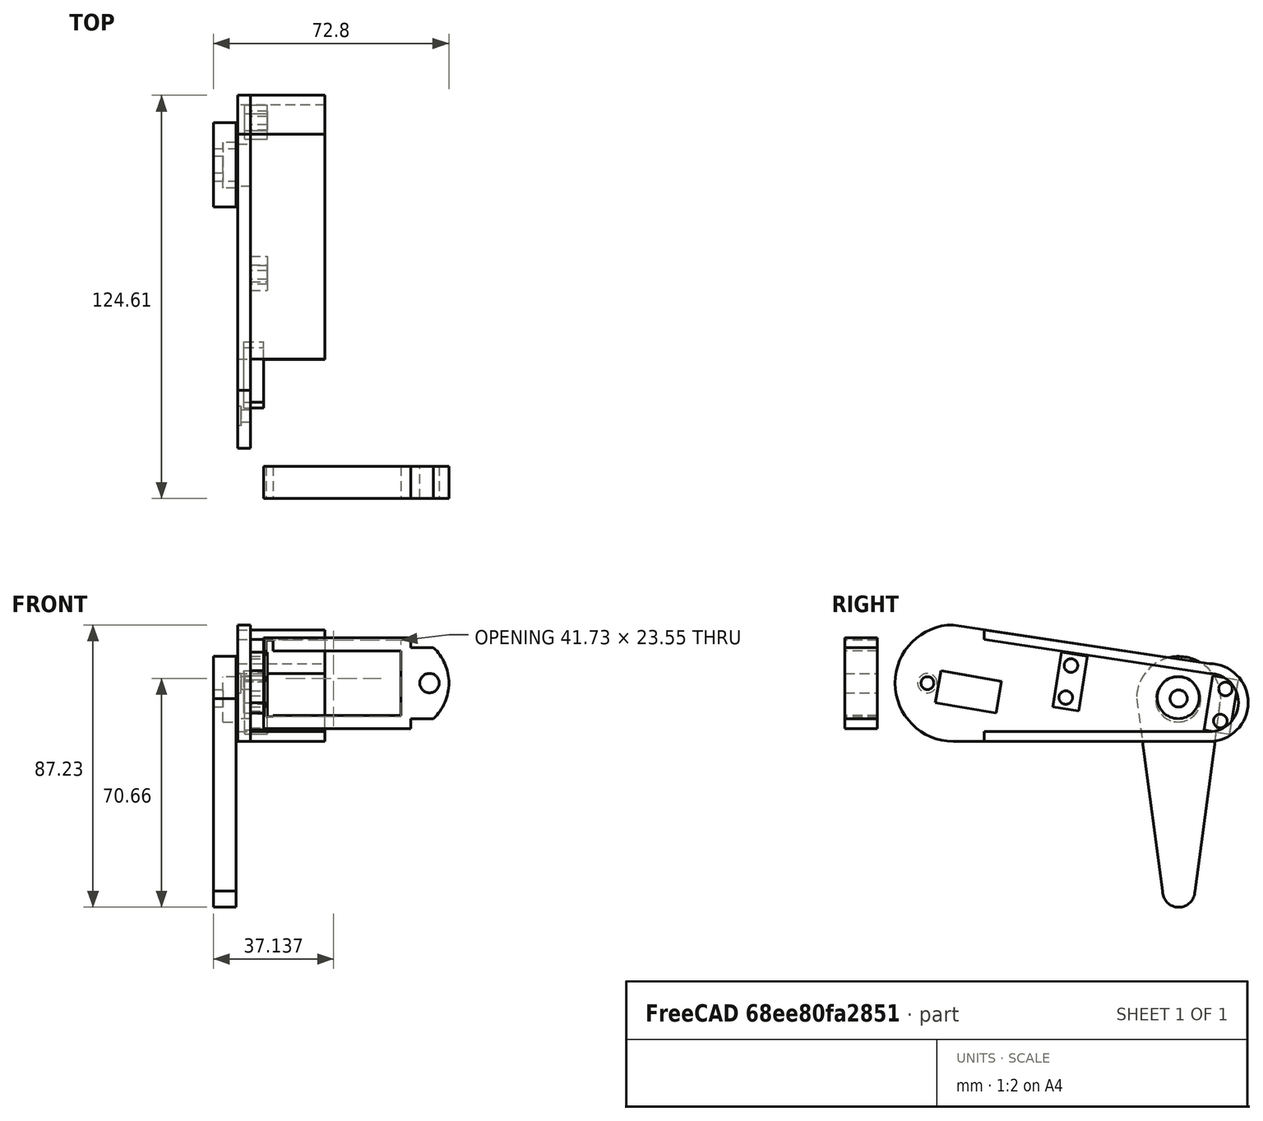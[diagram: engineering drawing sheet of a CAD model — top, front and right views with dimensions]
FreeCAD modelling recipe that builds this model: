
FCSTD DOCUMENT  (FreeCAD 0.20R29603 (Git))
Label: perro
License: All rights reserved
LicenseURL: http://en.wikipedia.org/wiki/All_rights_reserved
objects: Part::Cylinder×8, PartDesign::Pad×5, App::DocumentObjectGroup×5, Part::Cut×5, Sketcher::SketchObject×4, PartDesign::Body×4, Part::MultiFuse×4, Part::Box×4, Mesh::Feature×3, Spreadsheet::Sheet×1
note: 39 computed .brp shape members not serialized (recipe doc carries the construction recipe); baked Part::Feature solids carry a one-line shape summary decoded from their .brp

FEATURE [Mesh::Feature] nema17v0
  Placement = pos=(56,-128,65) rot=(-1,0,0;1.5708rad)
FEATURE [Sketcher::SketchObject] Sketch
  FullyConstrained = false
  MapMode = 5
  Placement = pos=(0,0,0) rot=(0.57735,0.57735,0.57735;2.0944rad)
  Support = -> [YZ_Plane]
  expr: Constraints[10] = Spreadsheet.AnchoPata
  expr: Constraints[12] = Spreadsheet.AnchoPata * 2
  expr: Constraints[14] = Spreadsheet.LargoRodillaExterior
  expr: Constraints[3] = Spreadsheet.AnchoRodilla
  expr: Constraints[5] = Spreadsheet.AnchoRodilla * 2
  sketch-geometry (5):
    g0: Circle CenterX=25.5525 CenterY=39.037 CenterZ=0 NormalX=0 NormalY=0 NormalZ=1 AngleXU=0 Radius=2.6446
    g1: LineSegment StartX=12.5525 StartY=39.0371 StartZ=0 EndX=20.5525 EndY=-20.4272 EndZ=0
    g2: LineSegment StartX=30.5525 StartY=-20.4272 StartZ=0 EndX=38.5525 EndY=39.0371 EndZ=0
    g3: ArcOfCircle CenterX=25.5525 CenterY=39.037 CenterZ=0 NormalX=0 NormalY=0 NormalZ=1 AngleXU=0 Radius=13 StartAngle=3.539e-06 EndAngle=3.14159
    g4: ArcOfCircle CenterX=25.5525 CenterY=-20.4272 CenterZ=0 NormalX=0 NormalY=0 NormalZ=1 AngleXU=0 Radius=5 StartAngle=3.1416 EndAngle=6.28318
  constraints (15):
    c: Coincident(g3,g1)
    c: Coincident(g3,g2)
    c: Coincident(g0,g3)
    c: Radius(g3) = 13
    c: Horizontal(g2,g1)
    c: DistanceX(g1,g2) = 26
    c: DistanceX(g0) = 25.5525
    c: DistanceY(g0) = 39.037
    c: Coincident(g4,g1)
    c: Coincident(g4,g2)
    c: Radius(g4) = 5
    c: Horizontal(g1,g2)
    c: DistanceX(g1,g2) = 10
    c: Equal(g2,g1)
    c: Distance(g2) = 60
FEATURE [PartDesign::Pad] Pad
  Direction = (1,-2e-16,3e-16)
  Length = 7
  Length2 = 10
  Placement = pos=(0,0,0) rot=(0.57735,0.57735,0.57735;2.0944rad)
  Profile = -> Sketch
  ReferenceAxis = -> Sketch [N_Axis]
  Type = 0
FEATURE [PartDesign::Body] Body  label="DebajoRodilla"
  Group = -> [Sketch,Pad]
  Origin = -> Origin
  Placement = pos=(10.5,-0.4,0.2) rot=(0,0,1;0rad)
  Tip = -> Pad
FEATURE [Spreadsheet::Sheet] Spreadsheet
  cells = A1=LargoParedesTrapecio; B1(LargoParedesTrapecio)=3; A2=RadioPataBase; B2(RadioPataBase)=12; D2=AnchoRodilla; E2(AnchoRodilla)=13; G2=LargoPiernaExterior; H2(LargoPiernaExterior)=20; J2=PiernaPiernaLargoExterior; K2(PiernaPiernaLargoExterior)=72; A3=RadioArcoInterior; B3(RadioArcoInterior)=15; D3=LargoRodillaExterior; E3(LargoRodillaExterior)=60; G3=LargoPiernaInterior; H3(LargoPiernaInterior)=20; J3=PiernaPiernaLargoInterior; K3(PiernaPiernaLargoInterior)=80; A4=AnchoPie; B4(AnchoPie)=17; D4=LargoRodillaInterior; E4(LargoRodillaInterior)=40; G4=AnchoPierna; H4(AnchoPierna)=15; J4=RadioPiernaSuperior; K4(RadioPiernaSuperior)=18; A5=LargoPieExterior; B5(LargoPieExterior)=10; D5=AnguloRodillaExterior; E5(AnguloRodillaExterior)=150; G5=RadioPierna; H5(RadioPierna)=9; J5=RadioPiernaInferior; K5(RadioPiernaInferior)=12; A6=LargoPieInterior; B6(LargoPieInterior)=10; D6=AnguloRodillaInterior; E6(AnguloRodillaInterior)=130; J6=AnguloPierna; K6(AnguloPierna)=20; A7=AnguloInteriorPie; B7(AnguloInteriorPie)=130; D7=AnchoPata; E7(AnchoPata)=5; A8=AnguloExteriorPie; B8(AnguloExteriorPie)=-150; A9=AnguloInteriorTrapecioPie; B9(AnguloInteriorTrapecioPie)=110; A10=BaseMenorTrapecio; B10(BaseMenorTrapecio)=7; A11=BaseMayorTrapecio; B11(BaseMayorTrapecio)=10; A12=DisTrapBaseMenACentCir; B12(DisTrapBaseMenACentCir)=20
FEATURE [Sketcher::SketchObject] Sketch002
  FullyConstrained = false
  MapMode = 5
  Placement = pos=(0,0,0) rot=(0.57735,0.57735,0.57735;2.0944rad)
  Support = -> [YZ_Plane002]
  expr: Constraints[10] = Spreadsheet.RadioPiernaInferior
  expr: Constraints[8] = Spreadsheet.PiernaPiernaLargoInterior
  expr: Constraints[9] = Spreadsheet.RadioPiernaSuperior
  sketch-geometry (9):
    g0: LineSegment StartX=-19.4851 StartY=0 StartZ=0 EndX=59.6098 EndY=0 EndZ=0
    g1: LineSegment StartX=-19.4851 StartY=36 StartZ=0 EndX=59.6098 EndY=24 EndZ=0
    g2: ArcOfCircle CenterX=59.6098 CenterY=12 CenterZ=0 NormalX=0 NormalY=0 NormalZ=1 AngleXU=0 Radius=12 StartAngle=4.71239 EndAngle=7.85398
    g3: ArcOfCircle CenterX=-19.4851 CenterY=18 CenterZ=0 NormalX=0 NormalY=0 NormalZ=1 AngleXU=0 Radius=18 StartAngle=1.5708 EndAngle=4.71239
    g4: Circle CenterX=50 CenterY=13.5287 CenterZ=0 NormalX=0 NormalY=0 NormalZ=1 AngleXU=0 Radius=6.5
    g5: GeomPoint X=68.8344 Y=19.675 Z=0
    g6: GeomPoint X=66.0715 Y=1.88833 Z=0
    g7: Circle CenterX=-27.4851 CenterY=18 CenterZ=0 NormalX=0 NormalY=0 NormalZ=1 AngleXU=0 Radius=1.98925
    g8: GeomPoint X=-37.4851 Y=18 Z=0
  constraints (25):
    c: Coincident(g2,g1)
    c: Coincident(g3,g1)
    c: Coincident(g3,g0)
    c: Vertical(g2,g1)
    c: Coincident(g2,g0)
    c: Vertical(g3,g1)
    c: Vertical(g3,g0)
    c: Vertical(g2,g0)
    c: Distance(g1) = 80
    c: Radius(g3) = 18
    c: Radius(g2) = 12
    c: PointOnObject(g0,g-1)
    c: PointOnObject(g0,g-1)
    c: Angle(g1,g-1) = 0.150568
    c: Angle(g1,g-1) = 0.150568
    c: PointOnObject(g5,g2)
    c: PointOnObject(g6,g2)
    c: Distance(g6,g5) = 18
    c: DistanceX(g4) = 50
    c: DistanceY(g4) = 13.5287
    c: Radius(g4) = 6.5
    c: Horizontal(g3,g7)
    c: PointOnObject(g8,g3)
    c: Horizontal(g8,g3)
    c: DistanceX(g8,g7) = 10
FEATURE [PartDesign::Pad] Pad002
  Direction = (1,-2e-16,3e-16)
  Length = 4
  Length2 = 10
  Placement = pos=(0,0,0) rot=(0.57735,0.57735,0.57735;2.0944rad)
  Profile = -> Sketch002
  ReferenceAxis = -> Sketch002 [N_Axis]
  Type = 0
FEATURE [PartDesign::Body] Body002  label="ArribaRodilla"
  Group = -> [Sketch002,Pad002]
  Origin = -> Origin002
  Placement = pos=(18,-25,26) rot=(0,0,1;0rad)
  Tip = -> Pad002
FEATURE [Mesh::Feature] MG995_dummy001  label="Rodilla"
  Placement = pos=(16.79,10.34,9.8) rot=(0.546223,0.635043,0.546223;2.01002rad)
FEATURE [Mesh::Feature] MG995_dummy002  label="Pierna"
  Placement = pos=(27,-62.5,12.5) rot=(0.57735,0.57735,0.57735;2.0944rad)
FEATURE [App::DocumentObjectGroup] Group  label="Motores"
  Group = -> [nema17v0,MG995_dummy001,MG995_dummy002]
FEATURE [Part::Cylinder] Cylinder
  Angle = 360
  AttacherType = Attacher::AttachEngine3D
  FirstAngle = 0
  Height = 5
  Placement = pos=(13.5,25,39) rot=(0,1,0;1.5708rad)
  Radius = 7
  SecondAngle = 0
FEATURE [Part::Cut] Cut
  Base = -> Body
  Tool = -> Cylinder
FEATURE [App::DocumentObjectGroup] Group001  label="DebajoRodilla001"
  Group = -> [Cut]
FEATURE [Part::Cylinder] Cylinder001
  Angle = 360
  AttacherType = Attacher::AttachEngine3D
  FirstAngle = 0
  Height = 10
  Placement = pos=(23,38,32.3) rot=(0,1,0;1.5708rad)
  Radius = 2.1
  SecondAngle = 0
FEATURE [Part::Cylinder] Cylinder002
  Angle = 360
  AttacherType = Attacher::AttachEngine3D
  FirstAngle = 0
  Height = 10
  Placement = pos=(23,39.6,42.2) rot=(0,1,0;1.5708rad)
  Radius = 2.1
  SecondAngle = 0
FEATURE [Part::MultiFuse] Fusion
  Placement = pos=(-1,0,0) rot=(0,0,1;0rad)
  Shapes = -> [Cylinder001,Cylinder002]
FEATURE [Part::Box] Box  label="Cube"
  AttacherType = Attacher::AttachEngine3D
  Height = 17
  Length = 7
  Placement = pos=(20.2,33,29.5) rot=(-1,0,0;0.15708rad)
  Width = 8
FEATURE [Part::Cut] Cut001
  Base = -> Box
  Tool = -> Fusion
FEATURE [App::DocumentObjectGroup] Group002  label="Soporte Servo"
  Group = -> [Cut001]
FEATURE [Part::Box] Box001  label="Cube001"
  AttacherType = Attacher::AttachEngine3D
  Height = 17
  Length = 7
  Placement = pos=(20.2,33,29.5) rot=(-1,0,0;0.15708rad)
  Width = 8
FEATURE [Part::Cylinder] Cylinder003
  Angle = 360
  AttacherType = Attacher::AttachEngine3D
  FirstAngle = 0
  Height = 10
  Placement = pos=(23,38,32.3) rot=(0,1,0;1.5708rad)
  Radius = 2.1
  SecondAngle = 0
FEATURE [Part::Cylinder] Cylinder004
  Angle = 360
  AttacherType = Attacher::AttachEngine3D
  FirstAngle = 0
  Height = 10
  Placement = pos=(23,39.6,42.2) rot=(0,1,0;1.5708rad)
  Radius = 2.1
  SecondAngle = 0
FEATURE [Part::MultiFuse] Fusion001
  Placement = pos=(-1,0,0) rot=(0,0,1;0rad)
  Shapes = -> [Cylinder003,Cylinder004]
FEATURE [Part::Cut] Cut002
  Base = -> Box001
  Tool = -> Fusion001
FEATURE [Part::Box] Box002  label="Cube002"
  AttacherType = Attacher::AttachEngine3D
  Height = 17
  Length = 7
  Placement = pos=(20.2,33,29.5) rot=(-1,0,0;0.15708rad)
  Width = 8
FEATURE [Part::Cylinder] Cylinder005
  Angle = 360
  AttacherType = Attacher::AttachEngine3D
  FirstAngle = 0
  Height = 10
  Placement = pos=(23,38,32.3) rot=(0,1,0;1.5708rad)
  Radius = 2.1
  SecondAngle = 0
FEATURE [Part::Cylinder] Cylinder006
  Angle = 360
  AttacherType = Attacher::AttachEngine3D
  FirstAngle = 0
  Height = 10
  Placement = pos=(23,39.6,42.2) rot=(0,1,0;1.5708rad)
  Radius = 2.1
  SecondAngle = 0
FEATURE [Part::MultiFuse] Fusion002
  Placement = pos=(-1,0,0) rot=(0,0,1;0rad)
  Shapes = -> [Cylinder005,Cylinder006]
FEATURE [Part::Cut] Cut003
  Base = -> Box002
  Placement = pos=(0,29.8756,81.7462) rot=(1,0,0;3.14159rad)
  Tool = -> Fusion002
FEATURE [Part::MultiFuse] Fusion003
  Shapes = -> [Cut003,Cut002,Body002]
FEATURE [Sketcher::SketchObject] Sketch004
  FullyConstrained = false
  MapMode = 5
  Placement = pos=(0,0,0) rot=(0.57735,0.57735,0.57735;2.0944rad)
  Support = -> [YZ_Plane004]
  expr: Constraints[2] = Spreadsheet.RadioPiernaInferior
  sketch-geometry (11):
    g0: ArcOfCircle CenterX=59.6097 CenterY=12 CenterZ=0 NormalX=0 NormalY=0 NormalZ=1 AngleXU=0 Radius=12 StartAngle=4.71239 EndAngle=7.85398
    g1: GeomPoint X=68.8339 Y=19.6755 Z=0
    g2: GeomPoint X=66.072 Y=1.88869 Z=0
    g3: ArcOfCircle CenterX=59.6097 CenterY=12 CenterZ=0 NormalX=0 NormalY=0 NormalZ=1 AngleXU=0 Radius=9 StartAngle=4.71239 EndAngle=7.85398
    g4: LineSegment StartX=-9.89505 StartY=31.4698 StartZ=0 EndX=-9.89505 EndY=34.4698 EndZ=0
    g5: LineSegment StartX=-10 StartY=3 StartZ=0 EndX=-10 EndY=0 EndZ=0
    g6: LineSegment StartX=-10 StartY=0 StartZ=0 EndX=59.6097 EndY=0 EndZ=0
    g7: LineSegment StartX=-10 StartY=3 StartZ=0 EndX=59.6097 EndY=3 EndZ=0
    g8: LineSegment StartX=-9.89505 StartY=31.4698 StartZ=0 EndX=59.6097 EndY=21 EndZ=0
    g9: LineSegment StartX=-9.89505 StartY=34.4698 StartZ=0 EndX=59.6097 EndY=24 EndZ=0
    g10: GeomPoint X=0.104952 Y=32.9635 Z=0
  constraints (27):
    c: Vertical(g0,g0)
    c: Vertical(g0,g0)
    c: Radius(g0) = 12
    c: PointOnObject(g0,g-1)
    c: PointOnObject(g1,g0)
    c: PointOnObject(g2,g0)
    c: Distance(g2,g1) = 18
    c: Vertical(g3,g0)
    c: Coincident(g3,g0)
    c: Vertical(g4)
    c: Vertical(g5)
    c: Coincident(g6,g5)
    c: Coincident(g6,g0)
    c: Horizontal(g6)
    c: Coincident(g7,g5)
    c: Coincident(g7,g3)
    c: Horizontal(g7)
    c: Coincident(g8,g4)
    c: Coincident(g8,g3)
    c: DistanceY(g5,g5) = 3
    c: DistanceY(g4,g4) = 3
    c: Coincident(g9,g4)
    c: Coincident(g9,g0)
    c: Equal(g8,g9)
    c: DistanceX(g5,g-1) = 10
    c: PointOnObject(g10,g9)
    c: DistanceX(g4,g10) = 10
FEATURE [PartDesign::Pad] Pad004
  Direction = (1,-2e-16,3e-16)
  Length = 27
  Length2 = 10
  Placement = pos=(0,0,0) rot=(0.57735,0.57735,0.57735;2.0944rad)
  Profile = -> Sketch004
  ReferenceAxis = -> Sketch004 [N_Axis]
  Type = 0
FEATURE [PartDesign::Body] Body004  label="ArribaRodilla002"
  Group = -> [Sketch004,Pad004]
  Origin = -> Origin004
  Placement = pos=(18,-25,26) rot=(0,0,1;0rad)
  Tip = -> Pad004
FEATURE [Part::Cylinder] Cylinder007
  Angle = 360
  AttacherType = Attacher::AttachEngine3D
  FirstAngle = 0
  Height = 10
  Placement = pos=(9,-52.5,44) rot=(0,1,0;1.5708rad)
  Radius = 3
  SecondAngle = 0
FEATURE [Part::Cut] Cut004
  Base = -> Fusion003
  Tool = -> Cylinder007
FEATURE [Part::Box] Box003  label="Cube003"
  AttacherType = Attacher::AttachEngine3D
  Height = 10
  Length = 6
  Placement = pos=(20,-50,38) rot=(-1,0,0;0.174533rad)
  Width = 19
FEATURE [App::DocumentObjectGroup] Group003  label="ArribaRodilla001"
  Group = -> [Cut004,Body004,Box003]
FEATURE [Sketcher::SketchObject] Sketch005
  FullyConstrained = false
  MapMode = 5
  Placement = pos=(0,0,0) rot=(1,0,0;1.5708rad)
  Support = -> [XZ_Plane006]
  sketch-geometry (17):
    g0: LineSegment StartX=16 StartY=14 StartZ=0 EndX=61.5 EndY=14 EndZ=0
    g1: LineSegment StartX=16 StartY=14 StartZ=0 EndX=16 EndY=-14 EndZ=0
    g2: LineSegment StartX=16 StartY=-14 StartZ=0 EndX=61.5 EndY=-14 EndZ=0
    g3: LineSegment StartX=61.5 StartY=14 StartZ=0 EndX=61.5 EndY=11 EndZ=0
    g4: LineSegment StartX=61.5 StartY=-14 StartZ=0 EndX=61.5 EndY=-11 EndZ=0
    g5: Circle CenterX=67.3 CenterY=0 CenterZ=0 NormalX=0 NormalY=0 NormalZ=1 AngleXU=0 Radius=3
    g6: LineSegment StartX=61.5 StartY=11 StartZ=0 EndX=68.5 EndY=11 EndZ=0
    g7: LineSegment StartX=61.5 StartY=-11 StartZ=0 EndX=68.5 EndY=-11 EndZ=0
    g8: ArcOfCircle CenterX=58.302 CenterY=0 CenterZ=0 NormalX=0 NormalY=0 NormalZ=1 AngleXU=0 Radius=15 StartAngle=5.45997 EndAngle=7.1064
    g9: LineSegment StartX=58.5 StartY=10 StartZ=0 EndX=19 EndY=10 EndZ=0
    g10: LineSegment StartX=19 StartY=-10 StartZ=0 EndX=58.5 EndY=-10 EndZ=0
    g11: LineSegment StartX=58.5 StartY=-10 StartZ=0 EndX=58.5 EndY=10 EndZ=0
    g12: LineSegment StartX=19 StartY=-10 StartZ=0 EndX=19 EndY=-10.21 EndZ=0
    g13: LineSegment StartX=19 StartY=-10.21 StartZ=0 EndX=16.7736 EndY=-10.3457 EndZ=0
    g14: LineSegment StartX=16.7736 StartY=-10.3457 StartZ=0 EndX=16.7736 EndY=13.2068 EndZ=0
    g15: LineSegment StartX=16.7736 StartY=13.2068 StartZ=0 EndX=19 EndY=13.2068 EndZ=0
    g16: LineSegment StartX=19 StartY=13.2068 StartZ=0 EndX=19 EndY=10 EndZ=0
  constraints (46):
    c: Coincident(g1,g0)
    c: Coincident(g2,g1)
    c: Horizontal(g2)
    c: Coincident(g3,g0)
    c: Vertical(g3)
    c: Coincident(g4,g2)
    c: Vertical(g4)
    c: Coincident(g6,g3)
    c: Horizontal(g6)
    c: Coincident(g7,g4)
    c: Horizontal(g7)
    c: Coincident(g8,g6)
    c: Coincident(g8,g7)
    c: Horizontal(g0)
    c: Vertical(g1)
    c: Equal(g4,g3)
    c: Equal(g6,g7)
    c: Equal(g0,g2)
    c: Coincident(g10,g11)
    c: Coincident(g11,g9)
    c: Horizontal(g9)
    c: PointOnObject(g8,g-1)
    c: PointOnObject(g5,g-1)
    c: DistanceX(g6,g6) = 7
    c: DistanceY(g3,g3) = 3
    c: Radius(g5) = 3
    c: Radius(g8) = 15
    c: Symmetric(g9,g10,g-1)
    c: Symmetric(g9,g10,g-1)
    c: DistanceX(g0,g0) = 45.5
    c: DistanceY(g9,g0) = 4
    c: DistanceX(g1,g10) = 3
    c: DistanceX(g9,g0) = 3
    c: DistanceX(g-1,g5) = 67.3
    c: DistanceX(g-1,g0) = 16
    c: Coincident(g12,g10)
    c: Vertical(g12)
    c: Coincident(g13,g12)
    c: Coincident(g14,g13)
    c: Vertical(g14)
    c: Coincident(g15,g14)
    c: Coincident(g16,g15)
    c: Coincident(g16,g9)
    c: Vertical(g16)
    c: Horizontal(g15)
    c: Distance(g4,g3) = 22
FEATURE [PartDesign::Pad] Pad005
  Direction = (0,-1,2e-16)
  Length = 10
  Length2 = 10
  Placement = pos=(0,0,0) rot=(1,0,0;1.5708rad)
  Profile = -> Sketch005
  ReferenceAxis = -> Sketch005 [N_Axis]
  Type = 0
FEATURE [PartDesign::Pad] Pad006
  BaseFeature = -> Pad005
  Direction = (0,-1,2e-16)
  Length = 10
  Length2 = 10
  Placement = pos=(0,0,0) rot=(1,0,0;1.5708rad)
  Profile = -> Sketch005
  ReferenceAxis = -> Sketch005 [N_Axis]
  TaperAngle = -1
  Type = 0
FEATURE [PartDesign::Body] Body005
  Group = -> [Sketch005,Pad005,Pad006]
  Origin = -> Origin005
  Placement = pos=(10,-68,44) rot=(0,0,1;0rad)
  Tip = -> Pad006
FEATURE [App::DocumentObjectGroup] Group004  label="Cadera"
  Group = -> [Body005]
